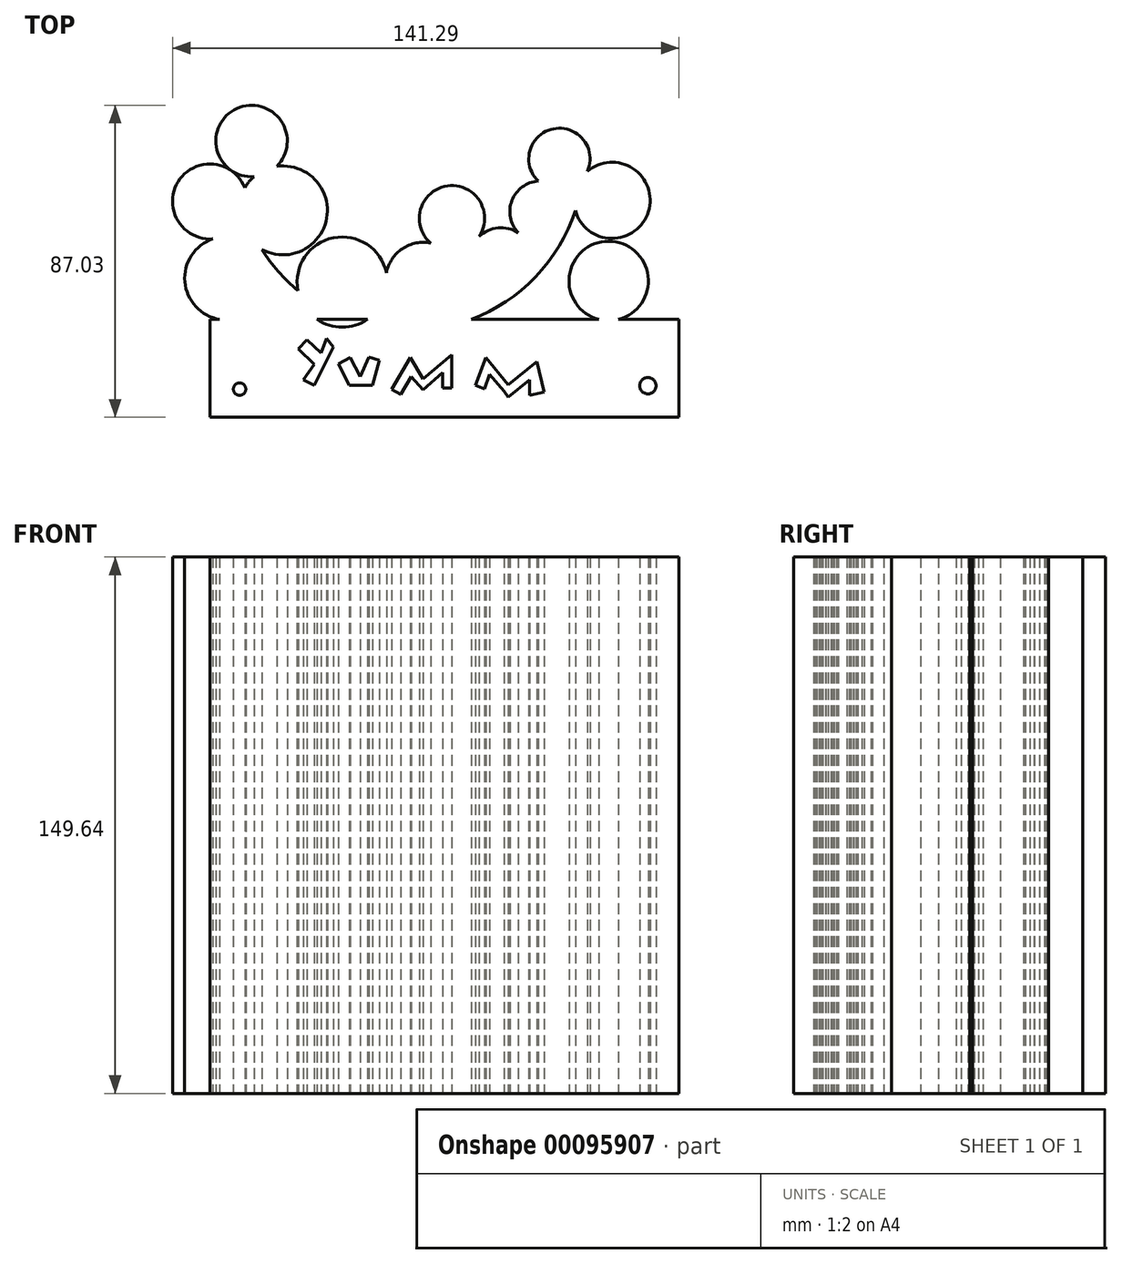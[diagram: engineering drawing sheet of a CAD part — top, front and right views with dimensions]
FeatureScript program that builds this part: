
annotation { "Feature Type Name" : "Feature", "Feature Type Description" : "" }
export const myFeature = defineFeature(function(context is Context, id is Id, definition is map)
    precondition{}
    {
        {
            var Q0;
            Q0=qCreatedBy(makeId("Top.planeOp"),FACE);
            var sketch = newSketch(context, id + "F0", { "sketchPlane" : qUnion([Q0])});
            skLineSegment(sketch, "E0", {"start": v(-59.47, -44.8) * mm, "end": v(71.35, -44.8) * mm});
            skLineSegment(sketch, "E1", {"start": v(-59.47, -44.8) * mm, "end": v(-59.47, -72.1) * mm});
            skLineSegment(sketch, "E2", {"start": v(-59.47, -72.1) * mm, "end": v(71.35, -72.1) * mm});
            skLineSegment(sketch, "E3", {"start": v(71.35, -48.25) * mm, "end": v(71.35, -72.1) * mm});
            skLineSegment(sketch, "E4", {"start": v(71.35, -48.25) * mm, "end": v(71.35, -44.8) * mm});
            skArc(sketch, "E5", {"start": v(-48.9, -17.72) * mm, "mid": v(1.77, -47.61) * mm, "end": v(44.27, -6.93) * mm});
            skCircle(sketch, "E6", {"center": v(-54.9, -33.32) * mm, "radius": 11.62 * mm});
            skCircle(sketch, "E7", {"center": v(-59.47, -11.9) * mm, "radius": 10.46 * mm});
            skCircle(sketch, "E8", {"center": v(-39.12, -14.39) * mm, "radius": 12.4 * mm});
            skCircle(sketch, "E9", {"center": v(-22.57, -34.37) * mm, "radius": 12.59 * mm});
            skCircle(sketch, "E10", {"center": v(0, -33.75) * mm, "radius": 10.45 * mm});
            skCircle(sketch, "E11", {"center": v(-47.86, 4.97) * mm, "radius": 9.96 * mm});
            skCircle(sketch, "E12", {"center": v(51.74, -34.06) * mm, "radius": 11.07 * mm});
            skCircle(sketch, "E13", {"center": v(52.68, -11.58) * mm, "radius": 10.62 * mm});
            skCircle(sketch, "E14", {"center": v(32.7, -14.7) * mm, "radius": 8.52 * mm});
            skCircle(sketch, "E15", {"center": v(21.77, -28.44) * mm, "radius": 9.18 * mm});
            skCircle(sketch, "E16", {"center": v(8.03, -16.58) * mm, "radius": 9.1 * mm});
            skCircle(sketch, "E17", {"center": v(38, 0) * mm, "radius": 8.55 * mm});
            skPoint(sketch, "E18.endSnap0", {"position": v(-59.47, -58.45) * mm});
            skPoint(sketch, "E19.endSnap0", {"position": v(55.49, -60.29) * mm});
            skLineSegment(sketch, "E20", {"start": v(62.69, -52.2) * mm, "end": v(62.69, -59.85) * mm});
            skCircle(sketch, "E21", {"center": v(62.69, -63.3) * mm, "radius": 2.28 * mm});
            skLineSegment(sketch, "E22", {"start": v(-34.84, -53.05) * mm, "end": v(-30.41, -57.31) * mm});
            skLineSegment(sketch, "E23", {"start": v(-25.06, -52.46) * mm, "end": v(-30.41, -63.16) * mm});
            skLineSegment(sketch, "E24", {"start": v(-20.55, -63.16) * mm, "end": v(-14.2, -63.16) * mm});
            skLineSegment(sketch, "E25", {"start": v(-14.2, -63.16) * mm, "end": v(-12.2, -56.14) * mm});
            skLineSegment(sketch, "E26", {"start": v(-34.84, -53.05) * mm, "end": v(-32.37, -50.48) * mm});
            skLineSegment(sketch, "E27", {"start": v(-32.37, -50.48) * mm, "end": v(-28.5, -54.2) * mm});
            skLineSegment(sketch, "E28", {"start": v(-28.5, -54.2) * mm, "end": v(-26.95, -50.12) * mm});
            skLineSegment(sketch, "E29", {"start": v(-26.95, -50.12) * mm, "end": v(-25.06, -52.46) * mm});
            skLineSegment(sketch, "E30", {"start": v(-30.41, -63.16) * mm, "end": v(-33.42, -61.66) * mm});
            skLineSegment(sketch, "E31", {"start": v(-30.41, -57.31) * mm, "end": v(-33.42, -61.66) * mm});
            skLineSegment(sketch, "E32", {"start": v(-20.55, -63.16) * mm, "end": v(-23.68, -57.25) * mm});
            skLineSegment(sketch, "E33", {"start": v(-23.68, -57.25) * mm, "end": v(-20.33, -55.48) * mm});
            skLineSegment(sketch, "E34", {"start": v(-20.33, -55.48) * mm, "end": v(-17.54, -60.76) * mm});
            skLineSegment(sketch, "E35", {"start": v(-12.2, -56.14) * mm, "end": v(-15.11, -55.3) * mm});
            skLineSegment(sketch, "E36", {"start": v(-15.11, -55.3) * mm, "end": v(-17.54, -60.76) * mm});
            skLineSegment(sketch, "E37", {"start": v(-8.8, -64.26) * mm, "end": v(-3.54, -55.42) * mm});
            skLineSegment(sketch, "E38", {"start": v(-3.54, -55.42) * mm, "end": v(0, -61.41) * mm});
            skLineSegment(sketch, "E39", {"start": v(0, -61.41) * mm, "end": v(7.9, -54.69) * mm});
            skLineSegment(sketch, "E40", {"start": v(7.9, -54.69) * mm, "end": v(7.9, -63.95) * mm});
            skLineSegment(sketch, "E41", {"start": v(-8.8, -64.26) * mm, "end": v(-6.27, -65.77) * mm});
            skLineSegment(sketch, "E42", {"start": v(-6.27, -65.77) * mm, "end": v(-3.29, -60.76) * mm});
            skLineSegment(sketch, "E43", {"start": v(-3.29, -60.76) * mm, "end": v(0, -64.5) * mm});
            skLineSegment(sketch, "E44", {"start": v(0, -64.5) * mm, "end": v(5.48, -59.68) * mm});
            skLineSegment(sketch, "E45", {"start": v(5.48, -59.68) * mm, "end": v(5.48, -63.95) * mm});
            skLineSegment(sketch, "E46", {"start": v(5.48, -63.95) * mm, "end": v(7.9, -63.95) * mm});
            skLineSegment(sketch, "E47", {"start": v(14.63, -63.23) * mm, "end": v(17.53, -55.42) * mm});
            skLineSegment(sketch, "E48", {"start": v(17.53, -55.42) * mm, "end": v(23.71, -63.05) * mm});
            skLineSegment(sketch, "E49", {"start": v(23.71, -63.05) * mm, "end": v(31.7, -56.58) * mm});
            skLineSegment(sketch, "E50", {"start": v(31.7, -56.58) * mm, "end": v(33.7, -65.04) * mm});
            skLineSegment(sketch, "E51", {"start": v(14.63, -63.23) * mm, "end": v(17.06, -64.13) * mm});
            skLineSegment(sketch, "E52", {"start": v(17.06, -64.13) * mm, "end": v(18.55, -60.11) * mm});
            skLineSegment(sketch, "E53", {"start": v(18.55, -60.11) * mm, "end": v(22.62, -64.86) * mm});
            skLineSegment(sketch, "E54", {"start": v(22.62, -64.86) * mm, "end": v(23.71, -66.5) * mm});
            skLineSegment(sketch, "E55", {"start": v(23.71, -66.5) * mm, "end": v(29.73, -61.62) * mm});
            skLineSegment(sketch, "E56", {"start": v(29.73, -61.62) * mm, "end": v(29.73, -65.95) * mm});
            skLineSegment(sketch, "E57", {"start": v(29.73, -65.95) * mm, "end": v(33.7, -65.04) * mm});
            skLineSegment(sketch, "E58", {"start": v(-51.66, -53.05) * mm, "end": v(-51.66, -60.88) * mm});
            skCircle(sketch, "E59", {"center": v(-51.21, -64.23) * mm, "radius": 1.75 * mm});
            skSolve(sketch);
        }
        {
            var Q0;
            Q0=sQuery(id+"F0.wireOp",EDGE,"E1");
            extrude(context, id + "F1", {"bodyType" : ToolBodyType.SURFACE, "surfaceEntities" : qUnion([Q0]), "depth" : 25.4 * mm});
        }
        {
            var Q0;
            Q0 = qSketchRegion(id + "F0", true);
            extrude(context, id + "F2", {"entities" : qUnion([Q0]), "depth" : 25.4 * mm});
        }
        {
            var Q0;
            Q0 = qSketchRegion(id + "F0", true);
            extrude(context, id + "F3", {"entities" : qUnion([Q0]), "operationType" : NewBodyOperationType.ADD, "endBound" : BoundingType.SYMMETRIC, "depth" : 149.64 * mm});
        }
    });
